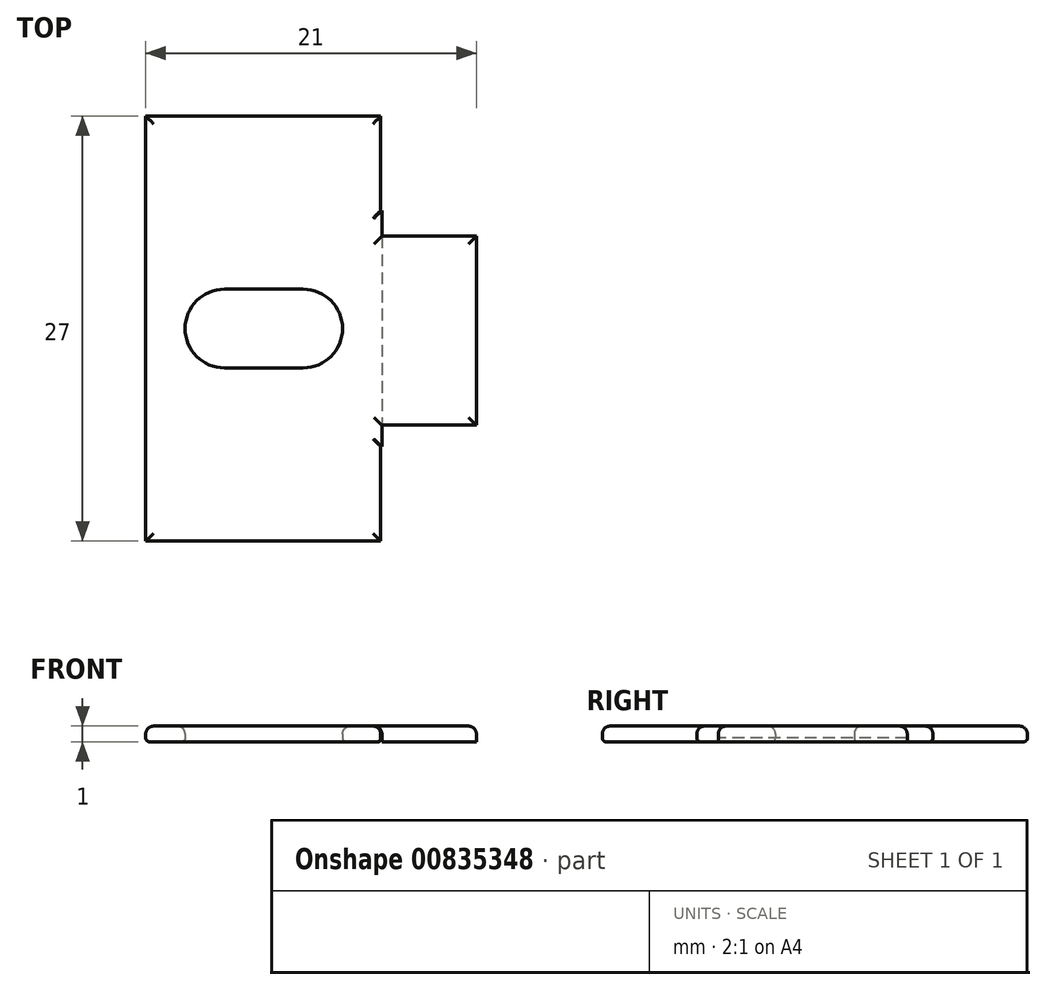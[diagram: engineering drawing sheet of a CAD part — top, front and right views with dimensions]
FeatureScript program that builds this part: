
annotation { "Feature Type Name" : "Feature", "Feature Type Description" : "" }
export const myFeature = defineFeature(function(context is Context, id is Id, definition is map)
    precondition{}
    {
        {
            var Q0;
            Q0=qCreatedBy(makeId("Top.planeOp"),FACE);
            var sketch = newSketch(context, id + "F0", { "sketchPlane" : qUnion([Q0])});
            skLineSegment(sketch, "E0.bottom", {"start": v(-7.5, 7.5) * mm, "end": v(7.5, 7.5) * mm});
            skLineSegment(sketch, "E0.top", {"start": v(-7.5, -7.5) * mm, "end": v(7.5, -7.5) * mm});
            skLineSegment(sketch, "E0.left", {"start": v(-7.5, 7.5) * mm, "end": v(-7.5, -7.5) * mm});
            skLineSegment(sketch, "E0.right", {"start": v(7.5, 7.5) * mm, "end": v(7.5, -7.5) * mm});
            skPoint(sketch, "E0.middle", {"position": v(0, 0) * mm});
            skLineSegment(sketch, "E1.bottom", {"start": v(-7.5, -7.5) * mm, "end": v(7.43, -7.5) * mm});
            skLineSegment(sketch, "E1.top", {"start": v(-7.5, -13.5) * mm, "end": v(7.43, -13.5) * mm});
            skLineSegment(sketch, "E1.left", {"start": v(-7.5, -7.5) * mm, "end": v(-7.5, -13.5) * mm});
            skLineSegment(sketch, "E1.right", {"start": v(7.43, -7.5) * mm, "end": v(7.43, -13.5) * mm});
            skLineSegment(sketch, "E2.bottom", {"start": v(-7.5, 7.5) * mm, "end": v(7.43, 7.5) * mm});
            skLineSegment(sketch, "E2.top", {"start": v(-7.5, 13.5) * mm, "end": v(7.43, 13.5) * mm});
            skLineSegment(sketch, "E2.left", {"start": v(-7.5, 7.5) * mm, "end": v(-7.5, 13.5) * mm});
            skLineSegment(sketch, "E2.right", {"start": v(7.43, 7.5) * mm, "end": v(7.43, 13.5) * mm});
            skLineSegment(sketch, "E3.bottom", {"start": v(-2.5, 2.5) * mm, "end": v(2.5, 2.5) * mm});
            skLineSegment(sketch, "E3.top", {"start": v(-2.5, -2.5) * mm, "end": v(2.5, -2.5) * mm});
            skLineSegment(sketch, "E3.left", {"start": v(-5, 0) * mm, "end": v(-5, 0) * mm});
            skLineSegment(sketch, "E3.right", {"start": v(5, 0) * mm, "end": v(5, 0) * mm});
            skPoint(sketch, "E4.visualSharp", {"position": v(5, 2.5) * mm});
            skArc(sketch, "E4.filletArc", {"start": v(5, 0) * mm, "mid": v(4.27, 1.77) * mm, "end": v(2.5, 2.5) * mm});
            skPoint(sketch, "E5.visualSharp", {"position": v(5, -2.5) * mm});
            skArc(sketch, "E5.filletArc", {"start": v(2.5, -2.5) * mm, "mid": v(4.27, -1.77) * mm, "end": v(5, 0) * mm});
            skPoint(sketch, "E6.visualSharp", {"position": v(-5, 2.5) * mm});
            skArc(sketch, "E6.filletArc", {"start": v(-2.5, 2.5) * mm, "mid": v(-4.27, 1.77) * mm, "end": v(-5, 0) * mm});
            skPoint(sketch, "E7.visualSharp", {"position": v(-5, -2.5) * mm});
            skArc(sketch, "E7.filletArc", {"start": v(-5, 0) * mm, "mid": v(-4.27, -1.77) * mm, "end": v(-2.5, -2.5) * mm});
            skLineSegment(sketch, "E8.bottom", {"start": v(7.5, -6.14) * mm, "end": v(13.5, -6.14) * mm});
            skLineSegment(sketch, "E8.top", {"start": v(7.5, 5.86) * mm, "end": v(13.5, 5.86) * mm});
            skLineSegment(sketch, "E8.left", {"start": v(7.5, -6.14) * mm, "end": v(7.5, 5.86) * mm});
            skLineSegment(sketch, "E8.right", {"start": v(13.5, -6.14) * mm, "end": v(13.5, 5.86) * mm});
            skLineSegment(sketch, "E9", {"start": v(13.5, -0.14) * mm, "end": v(7.5, -0.14) * mm, "construction": true});
            skLineSegment(sketch, "E10", {"start": v(-7.5, 0.13) * mm, "end": v(6.86, -0.14) * mm, "construction": true});
            skSolve(sketch);
        }
        {
            var Q0;
            Q0=makeQuery(id+"F0.imprint","IMPRINT",FACE,{"disambiguationData":[TD([[makeQuery(id+"F0.imprint","IMPRINT",EDGE,{"derivedFrom":sQuery(id+"F0.wireOp",EDGE,"E2.top")}),-1.0]])]});
            var Q1;
            {var subQ7=sQuery(id+"F0.wireOp",EDGE,"E0.left");Q1=makeQuery(id+"F0.imprint","IMPRINT",FACE,{"disambiguationData":[TD([[makeQuery(id+"F0.imprint","IMPRINT",EDGE,{"derivedFrom":subQ7}),1.0]])]});}
            var Q2;
            Q2=makeQuery(id+"F0.imprint","IMPRINT",FACE,{"disambiguationData":[TD([[makeQuery(id+"F0.imprint","IMPRINT",EDGE,{"derivedFrom":sQuery(id+"F0.wireOp",EDGE,"iIct8oxy-O5Oq-vDox-74YI-MHTgHuyWlBow.bottom")}),-1.0]])]});
            var Q3;
            Q3=makeQuery(id+"F0.imprint","IMPRINT",FACE,{"disambiguationData":[TD([[makeQuery(id+"F0.imprint","IMPRINT",EDGE,{"derivedFrom":sQuery(id+"F0.wireOp",EDGE,"E1.top")}),1.0]])]});
            extrude(context, id + "F1", {"entities" : qUnion([Q0, Q1, Q2, Q3]), "depth" : 1 * mm, "offsetDistance" : 25 * mm});
        }
        {
            var Q0;
            Q0=makeQuery(id+"F1.opExtrude","CAP_FACE",FACE,{"disambiguationData":[OSD([sQuery(id+"F0.wireOp",EDGE,"E0.bottom"),sQuery(id+"F0.wireOp",EDGE,"E0.top"),sQuery(id+"F0.wireOp",EDGE,"E0.left"),sQuery(id+"F0.wireOp",EDGE,"E0.right"),sQuery(id+"F0.wireOp",EDGE,"E1.top"),sQuery(id+"F0.wireOp",EDGE,"E1.left"),sQuery(id+"F0.wireOp",EDGE,"E1.right"),sQuery(id+"F0.wireOp",EDGE,"E2.top"),sQuery(id+"F0.wireOp",EDGE,"E2.left"),sQuery(id+"F0.wireOp",EDGE,"E2.right"),sQuery(id+"F0.wireOp",EDGE,"E3.bottom"),sQuery(id+"F0.wireOp",EDGE,"E3.top"),sQuery(id+"F0.wireOp",EDGE,"E4.filletArc"),sQuery(id+"F0.wireOp",EDGE,"E5.filletArc"),sQuery(id+"F0.wireOp",EDGE,"E6.filletArc"),sQuery(id+"F0.wireOp",EDGE,"E7.filletArc")])],"isStart":true});
            fillet(context, id + "F2", {"entities" : qUnion([Q0]), "radius" : 0.25 * mm, "tangentPropagation" : true, "allowEdgeOverflow" : false});
        }
        {
            var Q0;
            Q0=makeQuery(id+"F0.imprint","IMPRINT",FACE,{"disambiguationData":[TD([[makeQuery(id+"F0.imprint","IMPRINT",EDGE,{"derivedFrom":sQuery(id+"F0.wireOp",EDGE,"E3.bottom")}),-1.0]])]});
            extrude(context, id + "F3", {"entities" : qUnion([Q0]), "operationType" : NewBodyOperationType.REMOVE, "depth" : 1 * mm, "offsetDistance" : 25 * mm});
        }
        {
            var Q0;
            {var subQ2=sQuery(id+"F0.wireOp",EDGE,"E8.bottom");Q0=makeQuery(id+"F0.imprint","IMPRINT",FACE,{"disambiguationData":[TD([[makeQuery(id+"F0.imprint","IMPRINT",EDGE,{"derivedFrom":subQ2}),1.0]])]});}
            extrude(context, id + "F4", {"entities" : qUnion([Q0]), "operationType" : NewBodyOperationType.ADD, "depth" : 1 * mm, "offsetDistance" : 25 * mm});
        }
        {
            var Q0;
            {var subQ0=sQuery(id+"F0.wireOp",EDGE,"E0.right");Q0=makeQuery(id+"F4.boolean.opBoolean","MERGE",FACE,{"derivedFrom":[makeQuery(id+"F1.opExtrude","CAP_FACE",FACE,{"disambiguationData":[OSD([sQuery(id+"F0.wireOp",EDGE,"E0.bottom"),sQuery(id+"F0.wireOp",EDGE,"E0.top"),sQuery(id+"F0.wireOp",EDGE,"E0.left"),subQ0,sQuery(id+"F0.wireOp",EDGE,"E1.top"),sQuery(id+"F0.wireOp",EDGE,"E1.left"),sQuery(id+"F0.wireOp",EDGE,"E1.right"),sQuery(id+"F0.wireOp",EDGE,"E2.top"),sQuery(id+"F0.wireOp",EDGE,"E2.left"),sQuery(id+"F0.wireOp",EDGE,"E2.right"),sQuery(id+"F0.wireOp",EDGE,"E3.bottom"),sQuery(id+"F0.wireOp",EDGE,"E3.top"),sQuery(id+"F0.wireOp",EDGE,"E4.filletArc"),sQuery(id+"F0.wireOp",EDGE,"E5.filletArc"),sQuery(id+"F0.wireOp",EDGE,"E6.filletArc"),sQuery(id+"F0.wireOp",EDGE,"E7.filletArc")])],"isStart":false}),makeQuery(id+"F4.opExtrude","CAP_FACE",FACE,{"disambiguationData":[OSD([subQ0,sQuery(id+"F0.wireOp",EDGE,"E8.bottom"),sQuery(id+"F0.wireOp",EDGE,"E8.top"),sQuery(id+"F0.wireOp",EDGE,"E8.right")])],"isStart":false})]});}
            fillet(context, id + "F5", {"entities" : qUnion([Q0]), "radius" : 0.5 * mm, "tangentPropagation" : true, "allowEdgeOverflow" : false});
        }
    });
